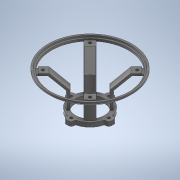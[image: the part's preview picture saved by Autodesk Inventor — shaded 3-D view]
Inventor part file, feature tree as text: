
AUTODESK INVENTOR PART (.ipt)
format: ipt  version: 2020 (Build 240168000, 168)  size: 471,040 bytes
history: native  units: mm
features: other x11, sketch x8, revolve x4, extrude x3, projected_geometry x3, pattern_circular x1, fillet x1
ambient origin geometry x8: Origin, YZ Plane, XZ Plane, XY Plane, X Axis, Y Axis, Z Axis, Center Point
bodies: Body1 (feature_tree)
feature tree (31):
  other  "Твердое тело1"
  extrude  "Выдавливание1"  Depth=34.0mm
  other  "РабПлоскость1"
  other  "РабОсь1"
  revolve  "Вращение1"
  sketch  "Эскиз3"
  other  "РабТочка1"
  extrude  "Выдавливание2"  Depth=45.0mm
  other  "РабТочка2"
  other  "РабТочка3"
  other  "РабТочка4"
  other  "РабПлоскость2"
  sketch  "Эскиз5"
  revolve  "Вращение2"
  revolve  "Вращение3"
  pattern_circular  "Круговой массив1"  Angle=45.0deg  [1 undecoded]
  extrude  "Выдавливание3"  Depth=3.3mm
  revolve  "Вращение4"
  sketch  "Эскиз8"
  fillet  "Сопряжение1"  Radius=9.0mm
  sketch  "Эскиз1"
  sketch  "Эскиз2"
  sketch  "Эскиз4"
  projected_geometry  "Спроецированная петля1"
  projected_geometry  "Спроецированная петля2"
  projected_geometry  "Спроецированная петля3"
  other  "РабПлоскость3"
  other  "РабПлоскость4"
  other  "РабПлоскость5"
  sketch  "Эскиз6"
  sketch  "Эскиз7"
note: 1 required parameter value undecoded (feature->parameter linkage not recoverable at this tier; creation-order binding heuristic only, values carry confidence <= 0.55)
